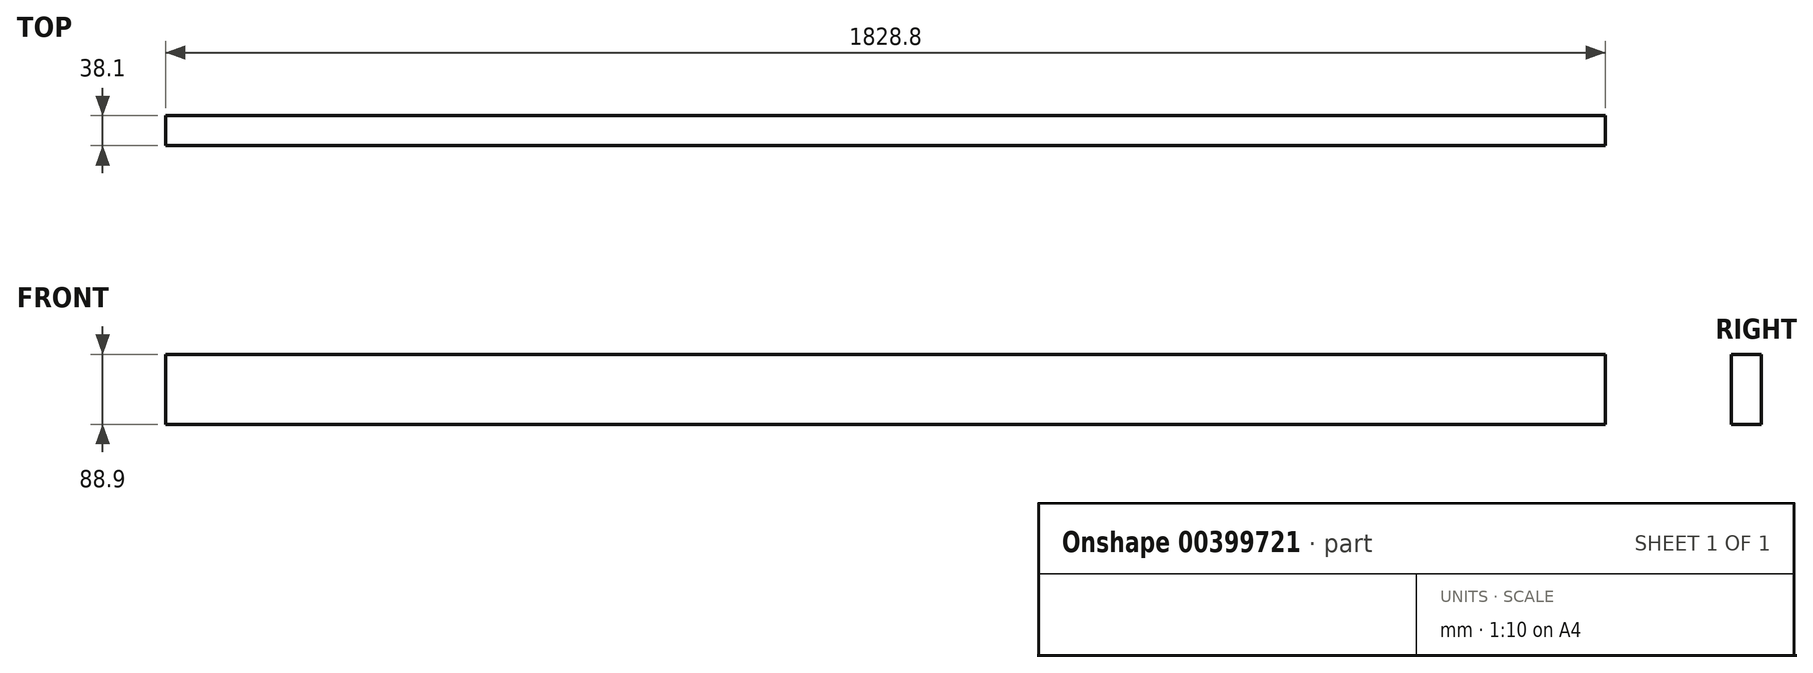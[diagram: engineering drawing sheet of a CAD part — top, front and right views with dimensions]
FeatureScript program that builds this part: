
annotation { "Feature Type Name" : "Feature", "Feature Type Description" : "" }
export const myFeature = defineFeature(function(context is Context, id is Id, definition is map)
    precondition{}
    {
        {
            var Q0;
            Q0=qCreatedBy(makeId("Right.planeOp"),FACE);
            var sketch = newSketch(context, id + "F0", { "sketchPlane" : qUnion([Q0])});
            skLineSegment(sketch, "E0.bottom", {"start": v(-19.05, -44.45) * mm, "end": v(19.05, -44.45) * mm});
            skLineSegment(sketch, "E0.top", {"start": v(-19.05, 44.45) * mm, "end": v(19.05, 44.45) * mm});
            skLineSegment(sketch, "E0.left", {"start": v(-19.05, -44.45) * mm, "end": v(-19.05, 44.45) * mm});
            skLineSegment(sketch, "E0.right", {"start": v(19.05, -44.45) * mm, "end": v(19.05, 44.45) * mm});
            skSolve(sketch);
        }
        {
            var Q0;
            Q0 = qSketchRegion(id + "F0", true);
            extrude(context, id + "F1", {"entities" : qUnion([Q0]), "endBound" : BoundingType.SYMMETRIC, "depth" : 1828.8 * mm});
        }
    });
